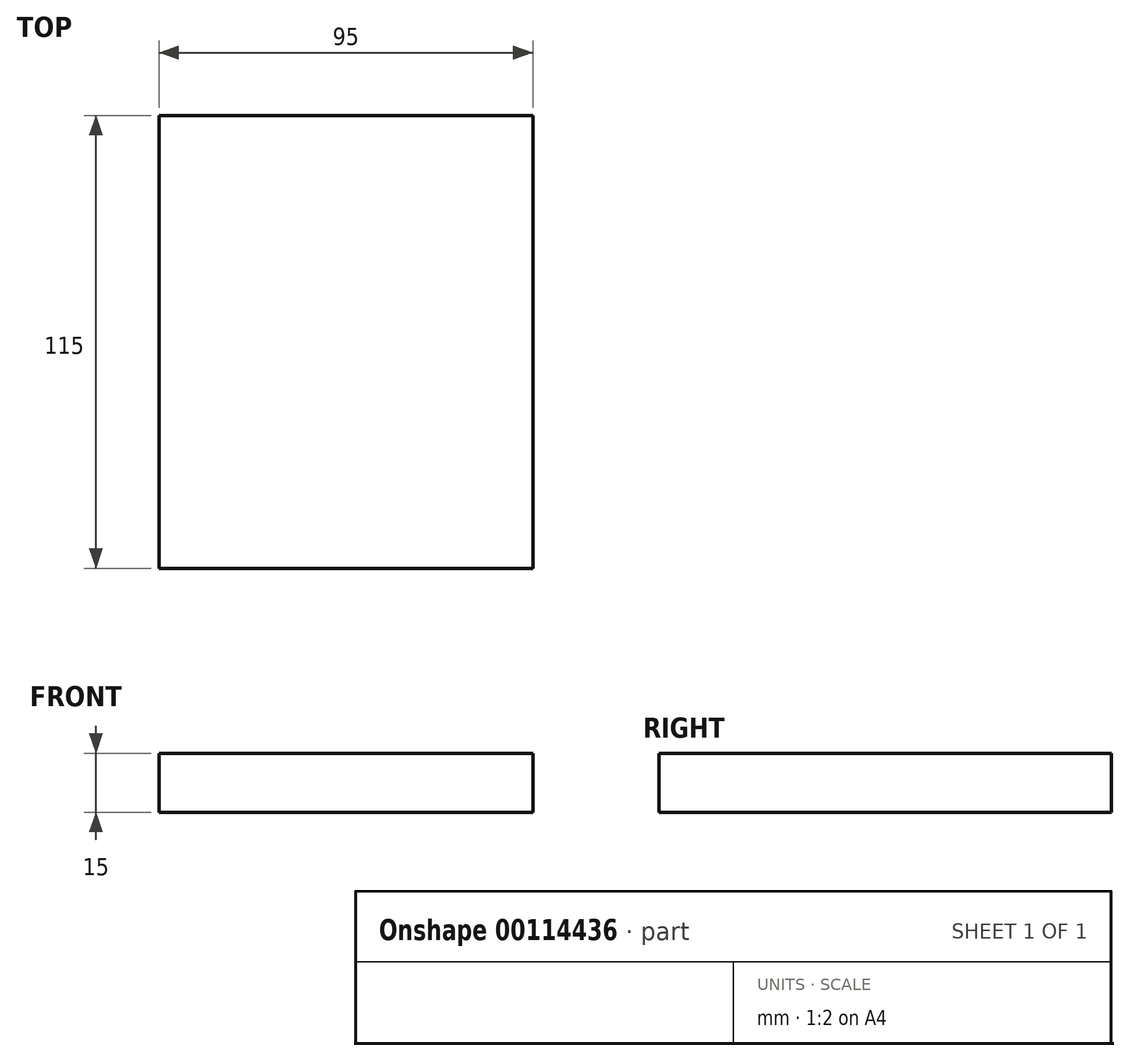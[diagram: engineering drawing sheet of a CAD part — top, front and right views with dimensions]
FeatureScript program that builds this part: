
annotation { "Feature Type Name" : "Feature", "Feature Type Description" : "" }
export const myFeature = defineFeature(function(context is Context, id is Id, definition is map)
    precondition{}
    {
        {
            var Q0;
            Q0=qCreatedBy(makeId("Top.planeOp"),FACE);
            var sketch = newSketch(context, id + "F0", { "sketchPlane" : qUnion([Q0])});
            skLineSegment(sketch, "E0.bottom", {"start": v(-47.5, -57.5) * mm, "end": v(47.5, -57.5) * mm});
            skLineSegment(sketch, "E0.top", {"start": v(-47.5, 57.5) * mm, "end": v(47.5, 57.5) * mm});
            skLineSegment(sketch, "E0.left", {"start": v(-47.5, -57.5) * mm, "end": v(-47.5, 57.5) * mm});
            skLineSegment(sketch, "E0.right", {"start": v(47.5, -57.5) * mm, "end": v(47.5, 57.5) * mm});
            skPoint(sketch, "E0.middle", {"position": v(0, 0) * mm});
            skSolve(sketch);
        }
        {
            var Q0;
            Q0 = qSketchRegion(id + "F0", true);
            extrude(context, id + "F1", {"entities" : qUnion([Q0]), "depth" : 15 * mm});
        }
    });
